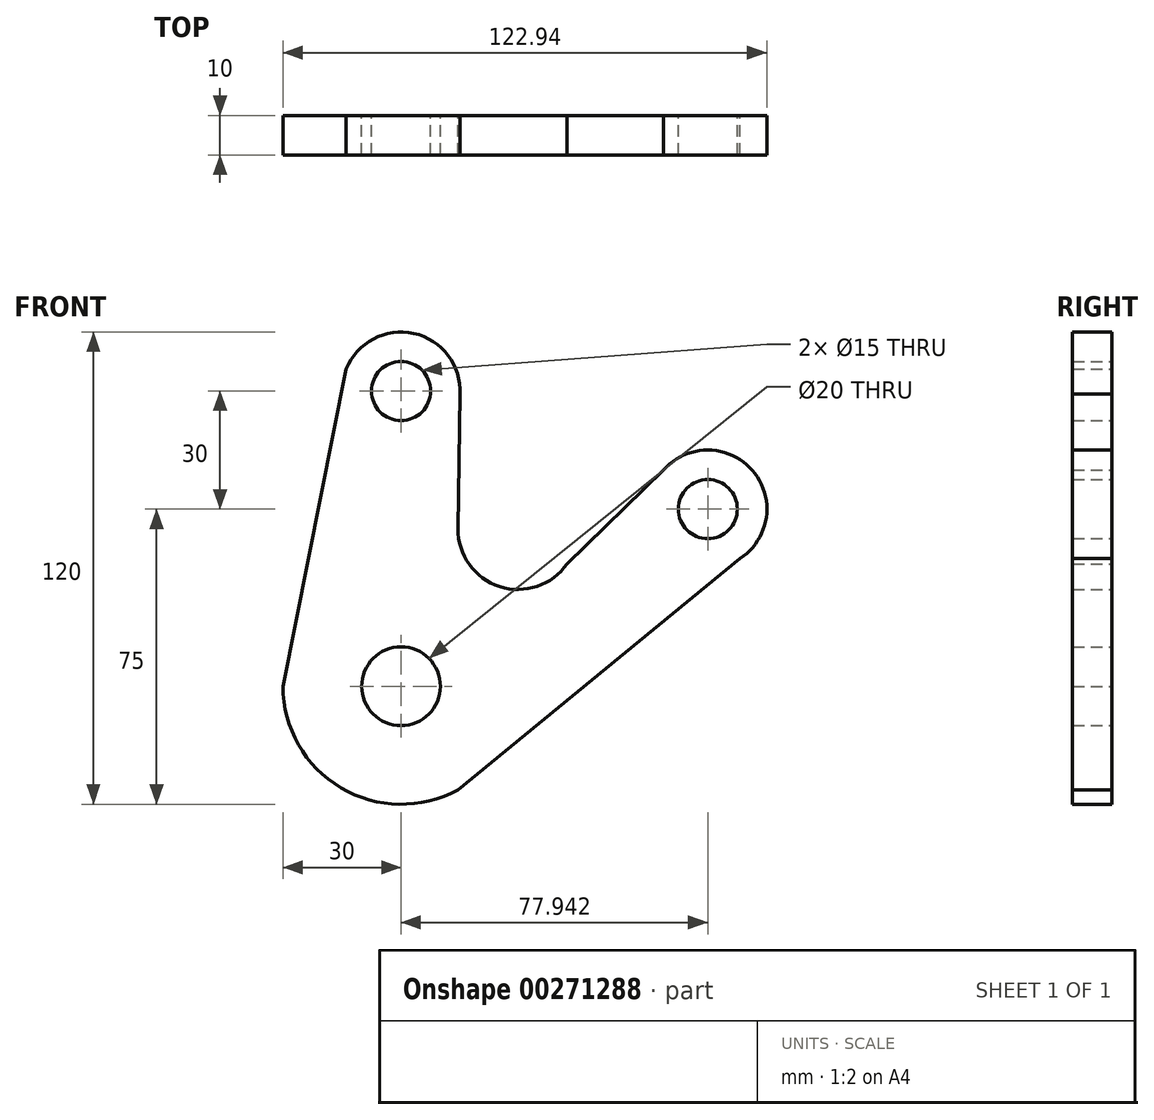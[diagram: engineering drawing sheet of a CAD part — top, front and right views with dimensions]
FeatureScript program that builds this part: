
annotation { "Feature Type Name" : "Feature", "Feature Type Description" : "" }
export const myFeature = defineFeature(function(context is Context, id is Id, definition is map)
    precondition{}
    {
        {
            var Q0;
            Q0=qCreatedBy(makeId("Front.planeOp"),FACE);
            var sketch = newSketch(context, id + "F0", { "sketchPlane" : qUnion([Q0])});
            skCircle(sketch, "E0", {"center": v(0, 0) * mm, "radius": 10 * mm});
            skLineSegment(sketch, "E1", {"start": v(0, 0) * mm, "end": v(0, 75) * mm, "construction": true});
            skCircle(sketch, "E2", {"center": v(0, 75) * mm, "radius": 7.5 * mm});
            skLineSegment(sketch, "E3", {"start": v(0, 0) * mm, "end": v(77.94, 45) * mm, "construction": true});
            skCircle(sketch, "E4", {"center": v(77.94, 45) * mm, "radius": 7.5 * mm});
            skArc(sketch, "E5", {"start": v(-30, 0) * mm, "mid": v(-15.28, -25.82) * mm, "end": v(14.44, -26.3) * mm});
            skArc(sketch, "E6", {"start": v(14.98, 74.18) * mm, "mid": v(3.23, 89.65) * mm, "end": v(-13.93, 80.56) * mm});
            skArc(sketch, "E7", {"start": v(86.13, 32.43) * mm, "mid": v(89.28, 54.82) * mm, "end": v(66.67, 54.9) * mm});
            skLineSegment(sketch, "E8", {"start": v(14.98, 74.18) * mm, "end": v(14.48, 40.07) * mm});
            skLineSegment(sketch, "E9", {"start": v(42.22, 31.1) * mm, "end": v(66.67, 54.9) * mm});
            skLineSegment(sketch, "E10", {"start": v(86.13, 32.43) * mm, "end": v(14.44, -26.3) * mm});
            skLineSegment(sketch, "E11", {"start": v(-30, 0) * mm, "end": v(-13.93, 80.56) * mm});
            skArc(sketch, "E12", {"start": v(14.48, 40.07) * mm, "mid": v(25.04, 25.34) * mm, "end": v(42.22, 31.1) * mm});
            skSolve(sketch);
        }
        {
            var Q0;
            Q0 = qSketchRegion(id + "F0", true);
            extrude(context, id + "F1", {"entities" : qUnion([Q0]), "depth" : 10 * mm});
        }
    });
